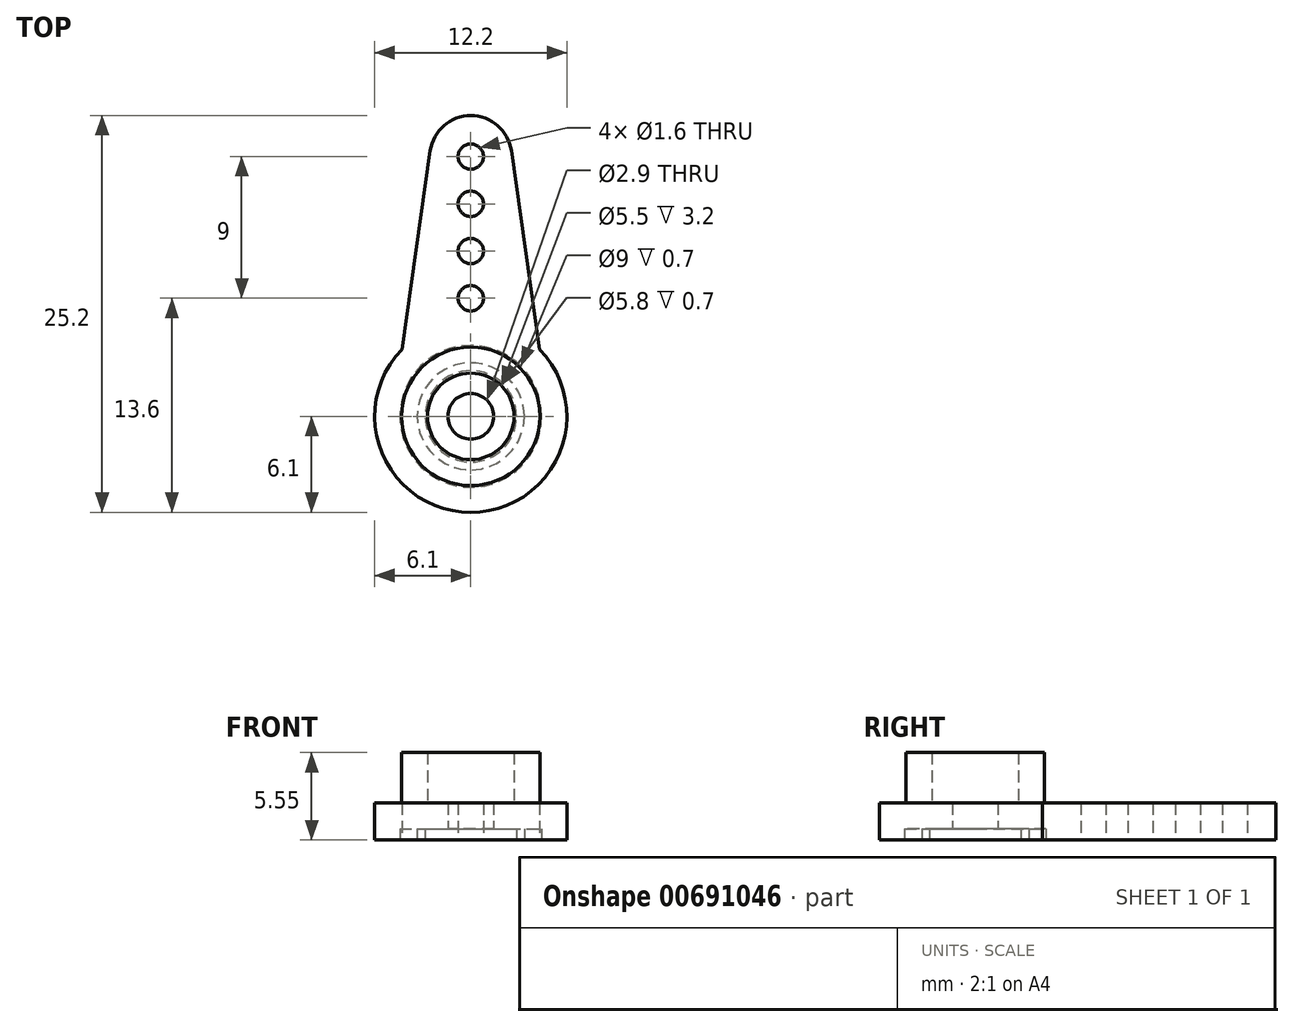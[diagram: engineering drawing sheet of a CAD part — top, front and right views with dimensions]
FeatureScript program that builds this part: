
annotation { "Feature Type Name" : "Feature", "Feature Type Description" : "" }
export const myFeature = defineFeature(function(context is Context, id is Id, definition is map)
    precondition{}
    {
        {
            var Q0;
            Q0=qCreatedBy(makeId("Top.planeOp"),FACE);
            var sketch = newSketch(context, id + "F0", { "sketchPlane" : qUnion([Q0])});
            skCircle(sketch, "E0", {"center": v(0, 0) * mm, "radius": 6.1 * mm});
            skCircle(sketch, "E1", {"center": v(0, 0) * mm, "radius": 4.4 * mm});
            skCircle(sketch, "E2", {"center": v(0, 0) * mm, "radius": 2.75 * mm});
            skCircle(sketch, "E3", {"center": v(0, 0) * mm, "radius": 1.45 * mm});
            skSolve(sketch);
        }
        {
            var Q0;
            Q0=makeQuery(id+"F0.imprint","IMPRINT",FACE,{"disambiguationData":[TD([[makeQuery(id+"F0.imprint","IMPRINT",EDGE,{"derivedFrom":sQuery(id+"F0.wireOp",EDGE,"E0")}),1.0]])]});
            var Q1;
            Q1=makeQuery(id+"F0.imprint","IMPRINT",FACE,{"disambiguationData":[TD([[makeQuery(id+"F0.imprint","IMPRINT",EDGE,{"derivedFrom":sQuery(id+"F0.wireOp",EDGE,"E1")}),1.0]])]});
            var Q2;
            Q2=makeQuery(id+"F0.imprint","IMPRINT",FACE,{"disambiguationData":[TD([[makeQuery(id+"F0.imprint","IMPRINT",EDGE,{"derivedFrom":sQuery(id+"F0.wireOp",EDGE,"E2")}),1.0]])]});
            extrude(context, id + "F1", {"entities" : qUnion([Q0, Q1, Q2]), "depth" : 2.35 * mm, "offsetDistance" : 25 * mm});
        }
        {
            var Q0;
            Q0=makeQuery(id+"F0.imprint","IMPRINT",FACE,{"disambiguationData":[TD([[makeQuery(id+"F0.imprint","IMPRINT",EDGE,{"derivedFrom":sQuery(id+"F0.wireOp",EDGE,"E1")}),1.0]])]});
            extrude(context, id + "F2", {"entities" : qUnion([Q0]), "operationType" : NewBodyOperationType.ADD, "depth" : 5.55 * mm, "offsetDistance" : 25 * mm});
        }
        {
            var Q0;
            Q0=qCreatedBy(makeId("Top.planeOp"),FACE);
            var sketch = newSketch(context, id + "F3", { "sketchPlane" : qUnion([Q0])});
            skLineSegment(sketch, "E4", {"start": v(-4.37, 4.25) * mm, "end": v(-2.57, 16.87) * mm});
            skLineSegment(sketch, "E5.MirrorCS", {"start": v(4.37, 4.25) * mm, "end": v(2.57, 16.87) * mm});
            skArc(sketch, "E6", {"start": v(2.57, 16.87) * mm, "mid": v(0, 19.1) * mm, "end": v(-2.57, 16.87) * mm});
            skCircle(sketch, "E7", {"center": v(0, 16.5) * mm, "radius": 0.8 * mm});
            skCircle(sketch, "E8", {"center": v(0, 13.5) * mm, "radius": 0.8 * mm});
            skCircle(sketch, "E9", {"center": v(0, 10.5) * mm, "radius": 0.8 * mm});
            skCircle(sketch, "E10", {"center": v(0, 7.5) * mm, "radius": 0.8 * mm});
            skArc(sketch, "E11", {"start": v(4.38, 4.25) * mm, "mid": v(0, 6.1) * mm, "end": v(-4.38, 4.25) * mm});
            skSolve(sketch);
        }
        {
            var Q0;
            Q0=makeQuery(id+"F3.imprint","IMPRINT",FACE,{"disambiguationData":[TD([[makeQuery(id+"F3.imprint","IMPRINT",EDGE,{"derivedFrom":sQuery(id+"F3.wireOp",EDGE,"E4")}),-1.0]])]});
            var Q1;
            {var subQ0=sQuery(id+"F0.wireOp",EDGE,"E0");Q1=makeQuery(id+"F2.boolean.opBoolean","SPLIT",FACE,{"disambiguationData":[TD([makeQuery(id+"F1.opExtrude","SWEPT_FACE",FACE,{"disambiguationData":[OSD([subQ0])]})])],"derivedFrom":makeQuery(id+"F1.opExtrude","CAP_FACE",FACE,{"disambiguationData":[OSD([subQ0,sQuery(id+"F0.wireOp",EDGE,"E3")])],"isStart":false})});}
            extrude(context, id + "F4", {"entities" : qUnion([Q0]), "operationType" : NewBodyOperationType.ADD, "endBound" : BoundingType.UP_TO_SURFACE, "depth" : 25 * mm, "endBoundEntityFace" : qUnion([Q1]), "offsetDistance" : 25 * mm});
        }
        {
            var Q0;
            Q0=qCreatedBy(makeId("Front.planeOp"),FACE);
            var sketch = newSketch(context, id + "F5", { "sketchPlane" : qUnion([Q0])});
            skLineSegment(sketch, "E12", {"start": v(0, 15.35) * mm, "end": v(0, -6.03) * mm, "construction": true});
            skSolve(sketch);
        }
        {
            var Q0;
            {var subQ0=sQuery(id+"F3.wireOp",EDGE,"E11");var subQ1=sQuery(id+"F3.wireOp",EDGE,"E10");var subQ2=sQuery(id+"F3.wireOp",EDGE,"E9");var subQ3=sQuery(id+"F3.wireOp",EDGE,"E8");var subQ4=sQuery(id+"F3.wireOp",EDGE,"E7");var subQ5=sQuery(id+"F3.wireOp",EDGE,"E6");var subQ6=sQuery(id+"F3.wireOp",EDGE,"E5.MirrorCS");var subQ7=sQuery(id+"F3.wireOp",EDGE,"E4");Q0=makeQuery(id+"FtbRCTXKljBNq9v_1.1.F4.boolean.opBoolean","MERGE",FACE,{"derivedFrom":[makeQuery(id+"F4.boolean.opBoolean","MERGE",FACE,{"derivedFrom":[makeQuery(id+"F1.opExtrude","CAP_FACE",FACE,{"disambiguationData":[OSD([sQuery(id+"F0.wireOp",EDGE,"E0"),sQuery(id+"F0.wireOp",EDGE,"E3")])],"isStart":true}),makeQuery(id+"F4.opExtrude","CAP_FACE",FACE,{"disambiguationData":[OSD([subQ7,subQ6,subQ5,subQ4,subQ3,subQ2,subQ1,subQ0])],"isStart":true})]}),makeQuery(id+"FtbRCTXKljBNq9v_1.1.F4.opExtrude","CAP_FACE",FACE,{"disambiguationData":[OSD([subQ7,subQ6,subQ5,subQ4,subQ3,subQ2,subQ1,subQ0])],"isStart":true})]});}
            var sketch = newSketch(context, id + "F6", { "sketchPlane" : qUnion([Q0])});
            skCircle(sketch, "E13", {"center": v(0, 0) * mm, "radius": 2.9 * mm});
            skCircle(sketch, "E14", {"center": v(0, 0) * mm, "radius": 4.5 * mm});
            skCircle(sketch, "E15", {"center": v(0, 0) * mm, "radius": 3.4 * mm});
            skSolve(sketch);
        }
        {
            var Q0;
            Q0=makeQuery(id+"F6.imprint","IMPRINT",FACE,{"disambiguationData":[TD([[makeQuery(id+"F6.imprint","IMPRINT",EDGE,{"derivedFrom":sQuery(id+"F6.wireOp",EDGE,"E14")}),1.0]])]});
            var Q1;
            Q1=makeQuery(id+"F6.imprint","IMPRINT",FACE,{"disambiguationData":[TD([[makeQuery(id+"F6.imprint","IMPRINT",EDGE,{"derivedFrom":sQuery(id+"F6.wireOp",EDGE,"E13")}),1.0]])]});
            extrude(context, id + "F7", {"entities" : qUnion([Q0, Q1]), "operationType" : NewBodyOperationType.REMOVE, "oppositeDirection" : true, "depth" : 0.7 * mm, "offsetDistance" : 25 * mm});
        }
    });
